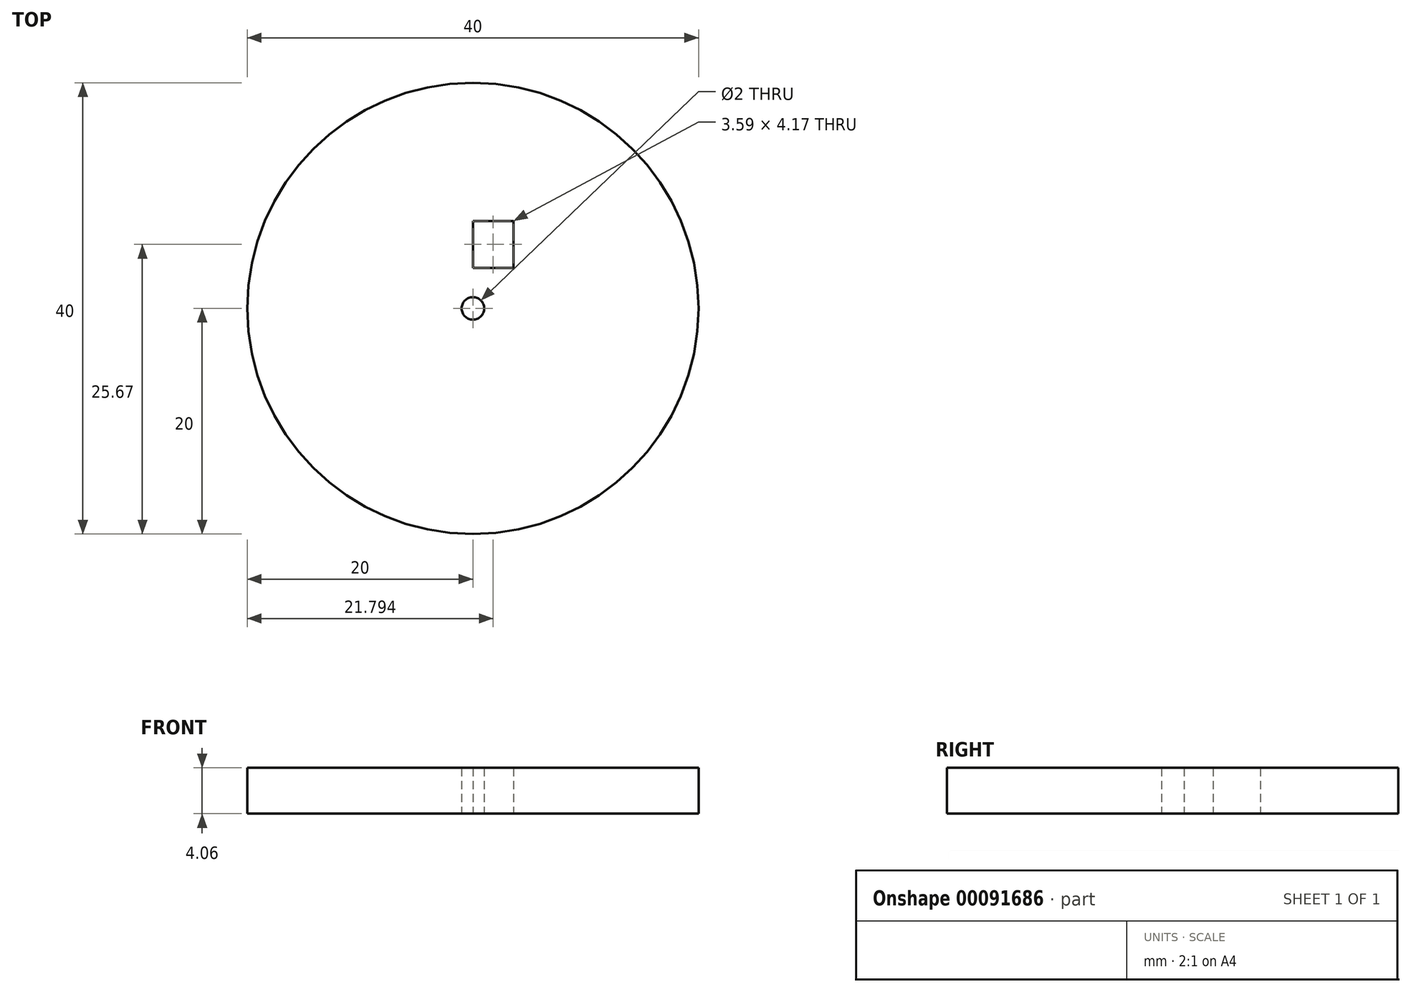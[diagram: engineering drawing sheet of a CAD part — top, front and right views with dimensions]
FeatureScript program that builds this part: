
annotation { "Feature Type Name" : "Feature", "Feature Type Description" : "" }
export const myFeature = defineFeature(function(context is Context, id is Id, definition is map)
    precondition{}
    {
        {
            var Q0;
            Q0=qCreatedBy(makeId("Top.planeOp"),FACE);
            var sketch = newSketch(context, id + "F0", { "sketchPlane" : qUnion([Q0])});
            skCircle(sketch, "E0", {"center": v(0, 0) * mm, "radius": 20 * mm});
            skPoint(sketch, "E1", {"position": v(0.3, -0.45) * mm});
            skCircle(sketch, "E2", {"center": v(0, 0) * mm, "radius": 1 * mm});
            skLineSegment(sketch, "E3.bottom", {"start": v(0, 7.75) * mm, "end": v(3.59, 7.75) * mm});
            skLineSegment(sketch, "E3.top", {"start": v(0, 3.59) * mm, "end": v(3.59, 3.59) * mm});
            skLineSegment(sketch, "E3.left", {"start": v(0, 7.75) * mm, "end": v(0, 3.59) * mm});
            skLineSegment(sketch, "E3.right", {"start": v(3.59, 7.75) * mm, "end": v(3.59, 3.59) * mm});
            skSolve(sketch);
        }
        {
            var Q0;
            Q0=makeQuery(id+"F0.imprint","IMPRINT",FACE,{"disambiguationData":[TD([[makeQuery(id+"F0.imprint","IMPRINT",EDGE,{"derivedFrom":sQuery(id+"F0.wireOp",EDGE,"E0")}),1.0]])]});
            extrude(context, id + "F1", {"entities" : qUnion([Q0]), "depth" : 4.06 * mm});
        }
    });
